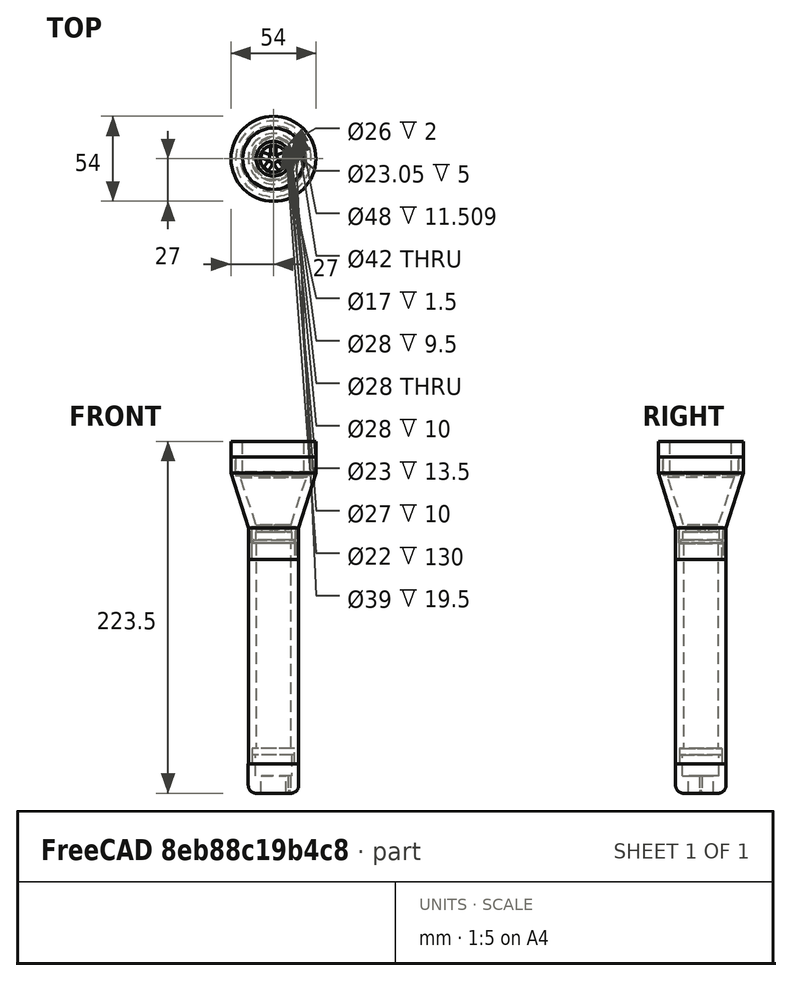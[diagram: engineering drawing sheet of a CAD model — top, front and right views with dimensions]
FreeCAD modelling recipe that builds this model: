
FCSTD DOCUMENT  (FreeCAD 0.19R)
Label: 21mm
License: All rights reserved
LicenseURL: http://en.wikipedia.org/wiki/All_rights_reserved
objects: TechDraw::DrawViewDimension×79, Sketcher::SketchObject×19, PartDesign::Pocket×7, PartDesign::Pad×6, TechDraw::DrawViewPart×6, TechDraw::DrawViewSection×6, PartDesign::Body×5, TechDraw::DrawSVGTemplate×5, TechDraw::DrawPage×5, PartDesign::Plane×3, PartDesign::Hole×3, PartDesign::ShapeBinder×2, PartDesign::Fillet×1, PartDesign::Revolution×1, PartDesign::PolarPattern×1
note: 65 computed .brp shape members not serialized (recipe doc carries the construction recipe); baked Part::Feature solids carry a one-line shape summary decoded from their .brp

FEATURE [Sketcher::SketchObject] Sketch
  MapMode = 5
  Support = -> [XY_Plane]
  sketch-geometry (3):
    g0: Circle CenterX=0 CenterY=0 CenterZ=0 NormalX=0 NormalY=0 NormalZ=1 AngleXU=0 Radius=11
    g1: Circle CenterX=0 CenterY=0 CenterZ=0 NormalX=0 NormalY=0 NormalZ=1 AngleXU=0 Radius=16
    g2: LineSegment [constr] StartX=0 StartY=16.2492 StartZ=0 EndX=0 EndY=22.2492 EndZ=0
  constraints (2):
    c: Radius(g0) = 11
    c: Radius(g1) = 16
FEATURE [PartDesign::Pad] Pad
  Length = 140
  Length2 = 100
  Profile = -> Sketch
  Type = 0
FEATURE [Sketcher::SketchObject] Sketch006
  MapMode = 5
  Placement = pos=(0,0,140) rot=(0,0,1;0rad)
  Support = -> [Pad]
  sketch-geometry (2):
    g0: Circle CenterX=-1e-16 CenterY=0 CenterZ=0 NormalX=0 NormalY=0 NormalZ=1 AngleXU=0 Radius=13.4656
    g1: Circle CenterX=0 CenterY=0 CenterZ=0 NormalX=0 NormalY=0 NormalZ=1 AngleXU=0 Radius=16
FEATURE [PartDesign::Plane] DatumPlane
  AttachmentOffset = pos=(0,-1,0) rot=(0,1,0;1.5708rad)
  Length = 225.248
  MapMode = 5
  Placement = pos=(0,-1,180) rot=(0,1,0;1.5708rad)
  ResizeMode = 0
  Width = 70.2485
FEATURE [Sketcher::SketchObject] Sketch003
  MapMode = 5
  Support = -> [XY_Plane001]
  sketch-geometry (1):
    g0: Circle CenterX=0.0013379 CenterY=-1.51036e-05 CenterZ=0 NormalX=0 NormalY=0 NormalZ=1 AngleXU=0 Radius=16.0028
FEATURE [PartDesign::Pad] Pad001
  Length = 18.5
  Length2 = 100
  Profile = -> Sketch003
  Reversed = true
  Type = 0
FEATURE [Sketcher::SketchObject] Sketch004
  MapMode = 5
  Placement = pos=(0,0,-25) rot=(1,0,0;3.14159rad)
  sketch-geometry (1):
    g0: Circle CenterX=0 CenterY=0 CenterZ=0 NormalX=0 NormalY=0 NormalZ=1 AngleXU=0 Radius=11
  constraints (1):
    c: Radius(g0) = 11  'plugdia'
FEATURE [Sketcher::SketchObject] Sketch005
  MapMode = 5
  Support = -> [Pad001]
  sketch-geometry (1):
    g0: Circle CenterX=0 CenterY=0 CenterZ=0 NormalX=0 NormalY=0 NormalZ=1 AngleXU=0 Radius=13.5
  constraints (1):
    c: Radius(g0) = 13.5
FEATURE [PartDesign::Pad] Pad002
  BaseFeature = -> Pad001
  Length = 6
  Length2 = 100
  Profile = -> Sketch005
  Type = 0
FEATURE [PartDesign::Fillet] Fillet
  Base = -> Pad002 [Edge3]
  BaseFeature = -> Pad002
  Radius = 5
FEATURE [Sketcher::SketchObject] Sketch027
  MapMode = 5
  Placement = pos=(0,0,-18.5) rot=(1,0,0;3.14159rad)
  Support = -> [Fillet]
  sketch-geometry (1):
    g0: Circle CenterX=0 CenterY=0 CenterZ=0 NormalX=0 NormalY=0 NormalZ=1 AngleXU=0 Radius=9.5
  constraints (1):
    c: Radius(g0) = 9.5
FEATURE [PartDesign::Hole] Hole
  BaseFeature = -> Fillet
  Depth = 31
  DepthType = 0
  Diameter = 16
  DrillPoint = 1
  DrillPointAngle = 118
  HoleCutCountersinkAngle = 90
  HoleCutDepth = 0
  HoleCutDiameter = 0
  HoleCutType = 0
  ModelActualThread = false
  Profile = -> Sketch027
  Tapered = false
  TaperedAngle = 90
  ThreadAngle = 0
  ThreadClass = 0
  ThreadCutOffInner = 0
  ThreadCutOffOuter = 0
  ThreadDirection = 0
  ThreadFit = 0
  ThreadPitch = 0
  ThreadSize = 0
  ThreadType = 0
  Threaded = false
FEATURE [Sketcher::SketchObject] Sketch028
  MapMode = 5
  Placement = pos=(0,0,0) rot=(1,0,0;3.14159rad)
  sketch-geometry (1):
    g0: Circle CenterX=0 CenterY=0 CenterZ=0 NormalX=0 NormalY=0 NormalZ=1 AngleXU=0 Radius=13.5
  constraints (1):
    c: Radius(g0) = 13.5
FEATURE [Sketcher::SketchObject] Sketch029
  MapMode = 5
  Placement = pos=(0,0,6) rot=(0,0,1;0rad)
  Support = -> [Hole]
FEATURE [Sketcher::SketchObject] Sketch030
  MapMode = 5
  Placement = pos=(0,0,6) rot=(0,0,1;0rad)
  Support = -> [Hole]
  sketch-geometry (1):
    g0: Circle CenterX=0 CenterY=0 CenterZ=0 NormalX=0 NormalY=0 NormalZ=1 AngleXU=0 Radius=11.5
  constraints (1):
    c: Radius(g0) = 11.5
FEATURE [PartDesign::Pocket] Pocket002
  BaseFeature = -> Hole
  Length = 13.5
  Length2 = 100
  Profile = -> Sketch030
  Type = 0
FEATURE [PartDesign::Pocket] Pocket001
  BaseFeature = -> Pad
  Length = 10
  Length2 = 100
  Profile = -> Sketch028
  Type = 0
FEATURE [PartDesign::Pocket] Pocket
  BaseFeature = -> Pocket001
  Length = 10
  Length2 = 100
  Profile = -> Sketch006
  Type = 0
FEATURE [PartDesign::Body] Body  label="batteryholder"
  Group = -> [Sketch,Pad,Sketch006,DatumPlane,Sketch028,Pocket001,Pocket]
  Origin = -> Origin
  Tip = -> Pocket
FEATURE [PartDesign::ShapeBinder] CopyPocket011
  Placement = pos=(0,-1,180) rot=(0,1,0;1.5708rad)
  TraceSupport = false
FEATURE [PartDesign::ShapeBinder] CopyPocket001
  TraceSupport = false
FEATURE [PartDesign::Plane] DatumPlane001
  AttachmentOffset = pos=(0,0,59) rot=(0,0,1;0rad)
  Length = 64.7976
  MapMode = 5
  Placement = pos=(0,0,249) rot=(0,0,1;0rad)
  ResizeMode = 0
  Support = -> [CopyPocket001]
  Width = 64.7986
FEATURE [Sketcher::SketchObject] Sketch018
  MapMode = 5
  Placement = pos=(0,0,249) rot=(0,0,1;0rad)
  Support = -> [DatumPlane001]
  sketch-geometry (1):
    g0: Circle CenterX=0 CenterY=0 CenterZ=0 NormalX=0 NormalY=0 NormalZ=1 AngleXU=0 Radius=27
  constraints (1):
    c: Radius(g0) = 27
FEATURE [PartDesign::Pad] Pad004
  Length = 10
  Length2 = 100
  Placement = pos=(0,0,249) rot=(0,0,1;0rad)
  Profile = -> Sketch018
  Type = 0
FEATURE [Sketcher::SketchObject] Sketch019
  MapMode = 5
  Placement = pos=(0,0,249) rot=(1,0,0;3.14159rad)
  Support = -> [Pad004]
  sketch-geometry (1):
    g0: Circle CenterX=0 CenterY=0 CenterZ=0 NormalX=0 NormalY=0 NormalZ=1 AngleXU=0 Radius=24
  constraints (1):
    c: Radius(g0) = 24
FEATURE [PartDesign::Pad] Pad005
  BaseFeature = -> Pad004
  Length = 9.5
  Length2 = 100
  Placement = pos=(0,0,249) rot=(0,0,1;0rad)
  Profile = -> Sketch019
  Type = 0
FEATURE [Sketcher::SketchObject] Sketch020
  MapMode = 5
  Placement = pos=(0,0,239.5) rot=(1,0,0;3.14159rad)
  Support = -> [Pad005]
  sketch-geometry (1):
    g0: Circle CenterX=0 CenterY=0 CenterZ=0 NormalX=0 NormalY=0 NormalZ=1 AngleXU=0 Radius=18
  constraints (1):
    c: Radius(g0) = 18
FEATURE [PartDesign::Hole] Hole001
  BaseFeature = -> Pad005
  Depth = 33
  DepthType = 0
  Diameter = 39
  DrillPoint = 1
  DrillPointAngle = 118
  HoleCutCountersinkAngle = 90
  HoleCutDepth = 0
  HoleCutDiameter = 0
  HoleCutType = 0
  ModelActualThread = false
  Placement = pos=(0,0,249) rot=(0,0,1;0rad)
  Profile = -> Sketch020
  Tapered = false
  TaperedAngle = 90
  ThreadAngle = 0
  ThreadClass = 0
  ThreadCutOffInner = 0
  ThreadCutOffOuter = 0
  ThreadDirection = 0
  ThreadFit = 0
  ThreadPitch = 0
  ThreadSize = 0
  ThreadType = 0
  Threaded = false
FEATURE [PartDesign::Body] Body004  label="linseholder001"
  Group = -> [CopyPocket011,DatumPlane001,CopyPocket001,Sketch018,Pad004,Sketch019,Pad005,Sketch020,Hole001]
  Origin = -> Origin004
  Placement = pos=(0,0,-54) rot=(0,0,1;0rad)
  Tip = -> Hole001
FEATURE [Sketcher::SketchObject] Sketch039
  MapMode = 5
  Placement = pos=(0,0,0) rot=(0.57735,0.57735,0.57735;2.0944rad)
  Support = -> [YZ_Plane005]
  sketch-geometry (16):
    g0: LineSegment StartX=27 StartY=195 StartZ=0 EndX=24 EndY=195 EndZ=0
    g1: LineSegment StartX=24 StartY=195 StartZ=0 EndX=24 EndY=183.491 EndZ=0
    g2: LineSegment StartX=24 StartY=183.491 StartZ=0 EndX=21 EndY=183.514 EndZ=0
    g3: LineSegment StartX=21 StartY=183.514 StartZ=0 EndX=21 EndY=182 EndZ=0
    g4: LineSegment StartX=21 StartY=182 StartZ=0 EndX=11 EndY=152 EndZ=0
    g5: LineSegment StartX=11 StartY=152 StartZ=0 EndX=8.5 EndY=152 EndZ=0
    g6: LineSegment StartX=8.5 StartY=152 StartZ=0 EndX=8.5 EndY=150.5 EndZ=0
    g7: LineSegment StartX=8.5 StartY=150.5 StartZ=0 EndX=14 EndY=150.5 EndZ=0
    g8: LineSegment StartX=14 StartY=150.5 StartZ=0 EndX=14 EndY=141 EndZ=0
    g9: LineSegment StartX=14 StartY=141 StartZ=0 EndX=14 EndY=140 EndZ=0
    g10: LineSegment StartX=14 StartY=140 StartZ=0 EndX=14 EndY=130 EndZ=0
    g11: LineSegment StartX=14 StartY=130 StartZ=0 EndX=16 EndY=130 EndZ=0
    g12: LineSegment StartX=16 StartY=130 StartZ=0 EndX=16 EndY=150 EndZ=0
    g13: LineSegment StartX=16 StartY=150 StartZ=0 EndX=27 EndY=185 EndZ=0
    g14: LineSegment StartX=27 StartY=185 StartZ=0 EndX=27 EndY=195 EndZ=0
    g15: LineSegment [constr] StartX=0 StartY=139 StartZ=0 EndX=13 EndY=139 EndZ=0
  constraints (15):
    c: Coincident(g0,g1)
    c: Coincident(g1,g2)
    c: Coincident(g2,g3)
    c: Coincident(g3,g4)
    c: Coincident(g4,g5)
    c: Coincident(g5,g6)
    c: Coincident(g6,g7)
    c: Coincident(g7,g8)
    c: Coincident(g8,g9)
    c: Coincident(g9,g10)
    c: Coincident(g10,g11)
    c: Coincident(g11,g12)
    c: Coincident(g12,g13)
    c: Coincident(g13,g14)
    c: Coincident(g14,g0)
FEATURE [PartDesign::Revolution] Revolution001
  Angle = 360
  Axis = (-3e-16,3e-16,1)
  Base = (0,0,0)
  Placement = pos=(0,0,0) rot=(0.57735,0.57735,0.57735;2.0944rad)
  Profile = -> Sketch039
  ReferenceAxis = -> Z_Axis005
  Reversed = true
FEATURE [PartDesign::Body] Body005  label="flashlighthead"
  Group = -> [Sketch039,Revolution001]
  Origin = -> Origin005
  Tip = -> Revolution001
FEATURE [PartDesign::Plane] DatumPlane002
  Length = 60
  MapMode = 45
  Placement = pos=(-8.73e-14,4.97e-14,150.5) rot=(0,0,1;0rad)
  ResizeMode = 0
  Support = -> [Revolution001]
  Width = 60
FEATURE [Sketcher::SketchObject] Sketch041
  MapMode = 5
  Placement = pos=(-8.73e-14,4.97e-14,150.5) rot=(0,0,1;0rad)
  Support = -> [DatumPlane002]
  sketch-geometry (1):
    g0: Circle CenterX=0 CenterY=0 CenterZ=0 NormalX=0 NormalY=0 NormalZ=1 AngleXU=0 Radius=14.0038
FEATURE [PartDesign::Pad] Pad006
  Length = 10
  Length2 = 100
  Placement = pos=(-1.02e-13,6.8e-14,150.5) rot=(0,0,1;0rad)
  Profile = -> Sketch041
  Reversed = true
  Type = 0
FEATURE [Sketcher::SketchObject] Sketch042
  MapMode = 5
  Placement = pos=(-1.02e-13,6.8e-14,140.5) rot=(1,0,0;3.14159rad)
  Support = -> [Pad006]
  sketch-geometry (1):
    g0: Circle CenterX=0 CenterY=0 CenterZ=0 NormalX=0 NormalY=0 NormalZ=1 AngleXU=0 Radius=13
  constraints (1):
    c: Radius(g0) = 13
FEATURE [PartDesign::Pocket] Pocket003
  BaseFeature = -> Pad006
  Length = 2
  Length2 = 100
  Placement = pos=(-1.02e-13,6.8e-14,150.5) rot=(0,0,1;0rad)
  Profile = -> Sketch042
  Type = 0
FEATURE [Sketcher::SketchObject] Sketch043
  MapMode = 5
  Placement = pos=(-1.02e-13,6.8e-14,142.5) rot=(1,0,0;3.14159rad)
  Support = -> [Pocket003]
  sketch-geometry (1):
    g0: Circle CenterX=0 CenterY=0 CenterZ=0 NormalX=0 NormalY=0 NormalZ=1 AngleXU=0 Radius=11.5274
FEATURE [PartDesign::Pocket] Pocket004
  BaseFeature = -> Pocket003
  Length = 5
  Length2 = 100
  Placement = pos=(-1.02e-13,6.8e-14,150.5) rot=(0,0,1;0rad)
  Profile = -> Sketch043
  Type = 0
FEATURE [Sketcher::SketchObject] Sketch044
  MapMode = 5
  Placement = pos=(-1.02e-13,6.8e-14,147.5) rot=(1,0,0;3.14159rad)
  Support = -> [Pocket004]
  sketch-geometry (4):
    g0: ArcOfCircle CenterX=-1e-16 CenterY=9.70622 CenterZ=0 NormalX=0 NormalY=0 NormalZ=1 AngleXU=0 Radius=1.77733 StartAngle=0 EndAngle=3.14159
    g1: ArcOfCircle CenterX=-1e-16 CenterY=4.33652 CenterZ=0 NormalX=0 NormalY=0 NormalZ=1 AngleXU=0 Radius=1.77733 StartAngle=3.14159 EndAngle=6.28319
    g2: LineSegment StartX=-1.77733 StartY=9.70622 StartZ=0 EndX=-1.77733 EndY=4.33652 EndZ=0
    g3: LineSegment StartX=1.77733 StartY=9.70622 StartZ=0 EndX=1.77733 EndY=4.33652 EndZ=0
  constraints (6):
    c: Tangent(g0,g3) = 1.5708
    c: Tangent(g0,g2) = -1.5708
    c: Tangent(g2,g1) = -1.5708
    c: Tangent(g3,g1) = 1.5708
    c: Vertical(g2)
    c: Equal(g0,g1)
FEATURE [PartDesign::Pocket] Pocket005
  BaseFeature = -> Pocket004
  Length = 5
  Length2 = 100
  Placement = pos=(-1.02e-13,6.8e-14,150.5) rot=(0,0,1;0rad)
  Profile = -> Sketch044
  Type = 0
FEATURE [PartDesign::PolarPattern] PolarPattern
  Angle = 360
  Axis = -> Sketch044 [N_Axis]
  BaseFeature = -> Pocket005
  Occurrences = 5
  Originals = -> [Pocket005]
  Placement = pos=(-1.02e-13,6.8e-14,150.5) rot=(0,0,1;0rad)
FEATURE [Sketcher::SketchObject] Sketch045
  MapMode = 5
  Placement = pos=(-1.02e-13,6.8e-14,150.5) rot=(0,0,1;0rad)
  Support = -> [PolarPattern]
  sketch-geometry (1):
    g0: Circle CenterX=0 CenterY=0 CenterZ=0 NormalX=0 NormalY=0 NormalZ=1 AngleXU=0 Radius=10.25
  constraints (1):
    c: Radius(g0) = 10.25
FEATURE [PartDesign::Pocket] Pocket006
  BaseFeature = -> PolarPattern
  Length = 1
  Length2 = 100
  Placement = pos=(-1.02e-13,6.8e-14,150.5) rot=(0,0,1;0rad)
  Profile = -> Sketch045
  Type = 0
FEATURE [PartDesign::Body] Body006  label="led-holder"
  Group = -> [DatumPlane002,Sketch041,Pad006,Sketch042,Pocket003,Sketch043,Pocket004,Sketch044,Pocket005,PolarPattern,Sketch045,Pocket006]
  Origin = -> Origin006
  Placement = pos=(0,0,0) rot=(0,0,-1;0.628319rad)
  Tip = -> Pocket006
FEATURE [Sketcher::SketchObject] Sketch046
  MapMode = 5
  Placement = pos=(0,0,-7.5) rot=(0,0,1;0rad)
  Support = -> [Pocket002]
  sketch-geometry (1):
    g0: Circle CenterX=10 CenterY=0 CenterZ=0 NormalX=0 NormalY=0 NormalZ=1 AngleXU=0 Radius=1
FEATURE [PartDesign::Hole] Hole002
  BaseFeature = -> Pocket002
  Depth = 10
  DepthType = 0
  Diameter = 1.75
  DrillPoint = 1
  DrillPointAngle = 118
  HoleCutCountersinkAngle = 90
  HoleCutDepth = 0
  HoleCutDiameter = 2
  HoleCutType = 0
  ModelActualThread = false
  Profile = -> Sketch046
  Tapered = false
  TaperedAngle = 90
  ThreadAngle = 60
  ThreadClass = 0
  ThreadCutOffInner = 0.0270633
  ThreadCutOffOuter = 0.0541266
  ThreadDirection = 1
  ThreadFit = 0
  ThreadPitch = 0.25
  ThreadSize = 6
  ThreadType = 2
  Threaded = true
FEATURE [PartDesign::Body] Body001  label="endcap"
  Group = -> [Sketch003,Pad001,Sketch004,Sketch005,Pad002,Fillet,Sketch027,Hole,Sketch029,Sketch030,Pocket002,Sketch046,Hole002]
  Origin = -> Origin001
  Tip = -> Hole002
FEATURE [TechDraw::DrawSVGTemplate] Template
  Height = 841
  Orientation = 1
  Width = 1189
FEATURE [TechDraw::DrawPage] Page
  KeepUpdated = true
  NextBalloonIndex = 1
  ProjectionType = 0
  Template = -> Template
FEATURE [TechDraw::DrawSVGTemplate] Template001
  EditableTexts = APPROVER_NAME=APPROVER NAME; AUTHOR_NAME=AUTHOR NAME; DATE=YYYY-MM-DD; DN=DN; OWNER_NAME=OWNER NAME; PM=PM; PN=PN; REVISION=REV A; RIGHTS=(R) DO NOT DUPLICATE THIS DRAWING TO THIRD PARTIES WITHOUT OWNER'S PERMISSION !; SCALE=M 1:2; SHEET=99 of 99; SIZE=A2; TITLELINE-1=FreeCAD; TOLERANCE=+/- ?
  Height = 420
  Orientation = 1
  Width = 594
FEATURE [TechDraw::DrawViewPart] View  label="Side View"
  CoarseView = false
  Direction = (-1,0,0)
  Focus = 100
  HardHidden = false
  IsoCount = 0
  IsoHidden = false
  IsoVisible = false
  LockPosition = false
  Perspective = false
  Rotation = 0
  Scale = 2
  ScaleType = 0
  SeamHidden = false
  SeamVisible = false
  SmoothHidden = false
  SmoothVisible = false
  Source = -> [Body]
  X = 105.013
  XDirection = (0,-1,0)
  Y = 202.99
FEATURE [TechDraw::DrawViewSection] SectionView  label="Section A - A"
  BaseView = -> View
  CoarseView = false
  CutSurfaceDisplay = 2
  Direction = (0,-1,0)
  FileGeomPattern = <path>
  FileHatchPattern = <path>
  Focus = 100
  FuseBeforeCut = true
  HardHidden = false
  HatchScale = 1
  IsoCount = 0
  IsoHidden = false
  IsoVisible = false
  LockPosition = false
  NameGeomPattern = Diamond
  Perspective = false
  Rotation = 0
  Scale = 2
  ScaleType = 0
  SeamHidden = false
  SeamVisible = false
  SectionDirection = 1
  SectionNormal = (0,-1,0)
  SectionOrigin = (0,0,70)
  SectionSymbol = A
  SmoothHidden = false
  SmoothVisible = false
  Source = -> [Body]
  X = 282.689
  XDirection = (1,0,0)
  Y = 201.911
FEATURE [TechDraw::DrawViewDimension] Dimension
  Arbitrary = false
  FormatSpec = %.1f
  Inverted = false
  LockPosition = false
  MeasureType = 1
  OverTolerance = 0
  References2D = -> [SectionView]
  Rotation = 0
  ScaleType = 0
  TheoreticalExact = false
  Type = 1
  UnderTolerance = 0
  X = -0.880671
  Y = 147.816
FEATURE [TechDraw::DrawViewDimension] Dimension001
  Arbitrary = false
  FormatSpec = %.1f
  Inverted = false
  LockPosition = false
  MeasureType = 1
  OverTolerance = 0
  References2D = -> [SectionView]
  Rotation = 0
  ScaleType = 0
  TheoreticalExact = false
  Type = 1
  UnderTolerance = 0
  X = 0
  Y = 155.302
FEATURE [TechDraw::DrawViewDimension] Dimension002
  Arbitrary = false
  FormatSpec = %.1f
  Inverted = false
  LockPosition = false
  MeasureType = 1
  OverTolerance = 0
  References2D = -> [SectionView]
  Rotation = 0
  ScaleType = 0
  TheoreticalExact = false
  Type = 1
  UnderTolerance = 0
  X = -0.550419
  Y = 164.254
FEATURE [TechDraw::DrawViewDimension] Dimension003
  Arbitrary = false
  FormatSpec = %.1f
  Inverted = false
  LockPosition = false
  MeasureType = 1
  OverTolerance = 0
  References2D = -> [SectionView]
  Rotation = 0
  ScaleType = 0
  TheoreticalExact = false
  Type = 2
  UnderTolerance = 0
  X = -41.1345
  Y = 131.871
FEATURE [TechDraw::DrawViewDimension] Dimension004
  Arbitrary = false
  FormatSpec = %.1f
  Inverted = false
  LockPosition = false
  MeasureType = 1
  OverTolerance = 0
  References2D = -> [SectionView]
  Rotation = 0
  ScaleType = 0
  TheoreticalExact = false
  Type = 2
  UnderTolerance = 0
  X = 44.9505
  Y = 127.768
FEATURE [TechDraw::DrawViewDimension] Dimension005
  Arbitrary = false
  FormatSpec = %.1f
  Inverted = false
  LockPosition = false
  MeasureType = 1
  OverTolerance = 0
  References2D = -> [SectionView]
  Rotation = 0
  ScaleType = 0
  TheoreticalExact = false
  Type = 2
  UnderTolerance = 0
  X = 36.1807
  Y = -0.330252
FEATURE [TechDraw::DrawViewDimension] Dimension006
  Arbitrary = false
  FormatSpec = %.1f
  Inverted = false
  LockPosition = false
  MeasureType = 1
  OverTolerance = 0
  References2D = -> [SectionView]
  Rotation = 0
  ScaleType = 0
  TheoreticalExact = false
  Type = 2
  UnderTolerance = 0
  X = -40.0361
  Y = -9.3395
FEATURE [TechDraw::DrawViewDimension] Dimension007
  Arbitrary = false
  FormatSpec = %.1f
  Inverted = false
  LockPosition = false
  MeasureType = 1
  OverTolerance = 0
  References2D = -> [SectionView]
  Rotation = 0
  ScaleType = 0
  TheoreticalExact = false
  Type = 1
  UnderTolerance = 0
  X = 0.330252
  Y = -150.788
FEATURE [TechDraw::DrawViewDimension] Dimension008
  Arbitrary = false
  FormatSpec = %.1f
  Inverted = false
  LockPosition = false
  MeasureType = 1
  OverTolerance = 0
  References2D = -> [SectionView]
  Rotation = 0
  ScaleType = 0
  TheoreticalExact = false
  Type = 2
  UnderTolerance = 0
  X = -20.9773
  Y = -129.009
FEATURE [TechDraw::DrawViewDimension] Dimension009
  Arbitrary = false
  FormatSpec = %.1f
  Inverted = false
  LockPosition = false
  MeasureType = 1
  OverTolerance = 0
  References2D = -> [SectionView]
  Rotation = 0
  ScaleType = 0
  TheoreticalExact = false
  Type = 1
  UnderTolerance = 0
  X = 0
  Y = -113.725
FEATURE [TechDraw::DrawViewDimension] Dimension010
  Arbitrary = false
  FormatSpec = %.1f
  Inverted = false
  LockPosition = false
  MeasureType = 1
  OverTolerance = 0
  References2D = -> [SectionView]
  Rotation = 0
  ScaleType = 0
  TheoreticalExact = false
  Type = 1
  UnderTolerance = 0
  X = 0.220168
  Y = -157.613
FEATURE [TechDraw::DrawViewDimension] Dimension011
  Arbitrary = false
  FormatSpec = %.1f
  Inverted = false
  LockPosition = false
  MeasureType = 1
  OverTolerance = 0
  References2D = -> [View]
  Rotation = 0
  ScaleType = 0
  TheoreticalExact = false
  Type = 1
  UnderTolerance = 0
  X = 2.85337
  Y = 153.886
FEATURE [TechDraw::DrawViewDimension] Dimension012
  Arbitrary = false
  FormatSpec = %.1f
  Inverted = false
  LockPosition = false
  MeasureType = 1
  OverTolerance = 0
  References2D = -> [View]
  Rotation = 0
  ScaleType = 0
  TheoreticalExact = false
  Type = 2
  UnderTolerance = 0
  X = -42.4009
  Y = 130.951
FEATURE [TechDraw::DrawPage] Page001
  KeepUpdated = true
  NextBalloonIndex = 1
  ProjectionType = 0
  Template = -> Template001
  Views = -> [View,SectionView,Dimension,Dimension001,Dimension002,Dimension003,Dimension004,Dimension005,Dimension006,Dimension007,Dimension008,Dimension009,Dimension010,Dimension011,Dimension012]
FEATURE [TechDraw::DrawSVGTemplate] Template002
  EditableTexts = AUTHOR_NAME=AUTHOR NAME; DN=DN; DRAWING_TITLE=DRAWING TITLE; FC-DATE=DD/MM/YYYY; FC-REV=REV A; FC-SC=SCALE; FC-SH=X / Y; FC-SI=A1; FreeCAD_DRAWING=FreeCAD DRAWING; PN=PN
  Height = 594
  Orientation = 1
  Width = 841
FEATURE [TechDraw::DrawPage] Page002
  KeepUpdated = true
  NextBalloonIndex = 1
  ProjectionType = 0
  Template = -> Template002
FEATURE [TechDraw::DrawSVGTemplate] Template003
  EditableTexts = APPROVER_NAME=APPROVER NAME; AUTHOR_NAME=AUTHOR NAME; DATE=YYYY-MM-DD; DN=DN; OWNER_NAME=OWNER NAME; PM=PM; PN=PN; REVISION=REV A; RIGHTS=(R) DO NOT DUPLICATE THIS DRAWING TO THIRD PARTIES WITHOUT OWNER'S PERMISSION !; SCALE=M 1:2; SHEET=99 of 99; SIZE=A2; TITLELINE-1=FreeCAD; TOLERANCE=+/- ?
  Height = 420
  Orientation = 1
  Width = 594
FEATURE [TechDraw::DrawViewPart] View001  label="Side View   "
  CoarseView = false
  Direction = (-1,0,0)
  Focus = 100
  HardHidden = false
  IsoCount = 0
  IsoHidden = false
  IsoVisible = false
  LockPosition = false
  Perspective = false
  Rotation = 0
  Scale = 2
  ScaleType = 0
  SeamHidden = false
  SeamVisible = false
  SmoothHidden = false
  SmoothVisible = false
  Source = -> [Body005]
  X = 132.111
  XDirection = (0,-1,0)
  Y = 297.733
FEATURE [TechDraw::DrawViewSection] SectionView001  label="Section A - A         "
  BaseView = -> View001
  CoarseView = false
  CutSurfaceDisplay = 2
  Direction = (0,-1,0)
  FileGeomPattern = <path>
  FileHatchPattern = <path>
  Focus = 100
  FuseBeforeCut = true
  HardHidden = false
  HatchScale = 1
  IsoCount = 0
  IsoHidden = false
  IsoVisible = false
  LockPosition = false
  NameGeomPattern = Diamond
  Perspective = false
  Rotation = 0
  Scale = 2
  ScaleType = 0
  SeamHidden = false
  SeamVisible = false
  SectionDirection = 1
  SectionNormal = (0,-1,0)
  SectionOrigin = (0,0,162.5)
  SectionSymbol = A
  SmoothHidden = false
  SmoothVisible = false
  Source = -> [Body005]
  X = 313.191
  XDirection = (1,0,0)
  Y = 297.219
FEATURE [TechDraw::DrawViewDimension] Dimension013
  Arbitrary = false
  FormatSpec = %.1f
  Inverted = false
  LockPosition = false
  MeasureType = 1
  OverTolerance = 0
  References2D = -> [SectionView001]
  Rotation = 0
  ScaleType = 0
  TheoreticalExact = false
  Type = 1
  UnderTolerance = 0
  X = -1.20591
  Y = 80.7974
FEATURE [TechDraw::DrawViewDimension] Dimension014
  Arbitrary = false
  FormatSpec = %.1f
  Inverted = false
  LockPosition = false
  MeasureType = 1
  OverTolerance = 0
  References2D = -> [SectionView001]
  Rotation = 0
  ScaleType = 0
  TheoreticalExact = false
  Type = 1
  UnderTolerance = 0
  X = -2.25746
  Y = 88.0956
FEATURE [TechDraw::DrawViewDimension] Dimension015
  Arbitrary = false
  FormatSpec = %.1f
  Inverted = false
  LockPosition = false
  MeasureType = 1
  OverTolerance = 0
  References2D = -> [View001]
  Rotation = 0
  ScaleType = 0
  TheoreticalExact = false
  Type = 2
  UnderTolerance = 0
  X = 58.1676
  Y = 55
FEATURE [TechDraw::DrawViewDimension] Dimension016
  Arbitrary = false
  FormatSpec = %.1f
  Inverted = false
  LockPosition = false
  MeasureType = 1
  OverTolerance = 0
  References2D = -> [View001]
  Rotation = 0
  ScaleType = 0
  TheoreticalExact = false
  Type = 1
  UnderTolerance = 0
  X = 0.520952
  Y = 76.6346
FEATURE [TechDraw::DrawViewDimension] Dimension017
  Arbitrary = false
  FormatSpec = %.1f
  Inverted = false
  LockPosition = false
  MeasureType = 1
  OverTolerance = 0
  References2D = -> [View001]
  Rotation = 0
  ScaleType = 0
  TheoreticalExact = false
  Type = 1
  UnderTolerance = 0
  X = 0.868254
  Y = -75.0717
FEATURE [TechDraw::DrawViewDimension] Dimension018
  Arbitrary = false
  FormatSpec = %.1f
  Inverted = false
  LockPosition = false
  MeasureType = 1
  OverTolerance = 0
  References2D = -> [View001]
  Rotation = 0
  ScaleType = 0
  TheoreticalExact = false
  Type = 2
  UnderTolerance = 0
  X = 36.3413
  Y = -44.6527
FEATURE [TechDraw::DrawViewDimension] Dimension019
  Arbitrary = false
  FormatSpec = %.1f
  Inverted = false
  LockPosition = false
  MeasureType = 1
  OverTolerance = 0
  References2D = -> [View001]
  Rotation = 0
  ScaleType = 0
  TheoreticalExact = false
  Type = 2
  UnderTolerance = 0
  X = 57.934
  Y = 8.9581
FEATURE [TechDraw::DrawViewDimension] Dimension020
  Arbitrary = false
  FormatSpec = %.1f
  Inverted = false
  LockPosition = false
  MeasureType = 1
  OverTolerance = 0
  References2D = -> [View001]
  Rotation = 0
  ScaleType = 0
  TheoreticalExact = false
  Type = 1
  UnderTolerance = 0
  X = 46.473
  Y = -19.347
FEATURE [TechDraw::DrawViewDimension] Dimension021
  Arbitrary = false
  FormatSpec = %.1f
  Inverted = false
  LockPosition = false
  MeasureType = 1
  OverTolerance = 0
  References2D = -> [SectionView001]
  Rotation = 0
  ScaleType = 0
  TheoreticalExact = false
  Type = 1
  UnderTolerance = 0
  X = -0.264201
  Y = 49.4251
FEATURE [TechDraw::DrawViewDimension] Dimension022
  Arbitrary = false
  FormatSpec = %.1f
  Inverted = false
  LockPosition = false
  MeasureType = 1
  OverTolerance = 0
  References2D = -> [SectionView001]
  Rotation = 0
  ScaleType = 0
  TheoreticalExact = false
  Type = 2
  UnderTolerance = 0
  X = 38.7415
  Y = 49.9149
FEATURE [TechDraw::DrawViewDimension] Dimension023
  Arbitrary = false
  FormatSpec = %.1f
  Inverted = false
  LockPosition = false
  MeasureType = 1
  OverTolerance = 0
  References2D = -> [SectionView001]
  Rotation = 0
  ScaleType = 0
  TheoreticalExact = false
  Type = 2
  UnderTolerance = 0
  X = -45.358
  Y = 54.0189
FEATURE [TechDraw::DrawViewDimension] Dimension024
  Arbitrary = false
  FormatSpec = %.1f
  Inverted = false
  LockPosition = false
  MeasureType = 1
  OverTolerance = 0
  References2D = -> [SectionView001]
  Rotation = 0
  ScaleType = 0
  TheoreticalExact = false
  Type = 1
  UnderTolerance = 0
  X = 9.64335
  Y = -3.56272
FEATURE [TechDraw::DrawViewDimension] Dimension025
  Arbitrary = false
  FormatSpec = %.1f
  Inverted = false
  LockPosition = false
  MeasureType = 1
  OverTolerance = 0
  References2D = -> [SectionView001]
  Rotation = 0
  ScaleType = 0
  TheoreticalExact = false
  Type = 2
  UnderTolerance = 0
  X = 53.4003
  Y = 13.8877
FEATURE [TechDraw::DrawViewDimension] Dimension026
  Arbitrary = false
  FormatSpec = %.1f
  Inverted = false
  LockPosition = false
  MeasureType = 1
  OverTolerance = 0
  References2D = -> [SectionView001]
  Rotation = 0
  ScaleType = 0
  TheoreticalExact = false
  Type = 1
  UnderTolerance = 0
  X = 6.73713
  Y = -28.3593
FEATURE [TechDraw::DrawViewDimension] Dimension027
  Arbitrary = false
  FormatSpec = %.1f
  Inverted = false
  LockPosition = false
  MeasureType = 1
  OverTolerance = 0
  References2D = -> [SectionView001]
  Rotation = 0
  ScaleType = 0
  TheoreticalExact = false
  Type = 2
  UnderTolerance = 0
  X = -12.1123
  Y = -13.253
FEATURE [TechDraw::DrawViewDimension] Dimension028
  Arbitrary = false
  FormatSpec = %.1f
  Inverted = false
  LockPosition = false
  MeasureType = 1
  OverTolerance = 0
  References2D = -> [SectionView001]
  Rotation = 0
  ScaleType = 0
  TheoreticalExact = false
  Type = 1
  UnderTolerance = 0
  X = -0.396302
  Y = -79.7953
FEATURE [TechDraw::DrawViewDimension] Dimension029
  Arbitrary = false
  FormatSpec = %.1f
  Inverted = false
  LockPosition = false
  MeasureType = 1
  OverTolerance = 0
  References2D = -> [SectionView001]
  Rotation = 0
  ScaleType = 0
  TheoreticalExact = false
  Type = 1
  UnderTolerance = 0
  X = 2.24571
  Y = -87.9855
FEATURE [TechDraw::DrawViewDimension] Dimension030
  Arbitrary = false
  FormatSpec = %.1f
  Inverted = false
  LockPosition = false
  MeasureType = 1
  OverTolerance = 0
  References2D = -> [SectionView001]
  Rotation = 0
  ScaleType = 0
  TheoreticalExact = false
  Type = 2
  UnderTolerance = 0
  X = -61.3263
  Y = -44.6037
FEATURE [TechDraw::DrawViewDimension] Dimension031
  Arbitrary = false
  FormatSpec = %.1f
  Inverted = false
  LockPosition = false
  MeasureType = 1
  OverTolerance = 0
  References2D = -> [SectionView001]
  Rotation = 0
  ScaleType = 0
  TheoreticalExact = false
  Type = 2
  UnderTolerance = 0
  X = -61.362
  Y = 9.4716
FEATURE [TechDraw::DrawViewDimension] Dimension032
  Arbitrary = false
  FormatSpec = %.1f
  Inverted = false
  LockPosition = false
  MeasureType = 1
  OverTolerance = 0
  References2D = -> [SectionView001]
  Rotation = 0
  ScaleType = 0
  TheoreticalExact = false
  Type = 2
  UnderTolerance = 0
  X = -61.2655
  Y = 55.9247
FEATURE [TechDraw::DrawViewDimension] Dimension033
  Arbitrary = false
  FormatSpec = %.1f
  Inverted = false
  LockPosition = false
  MeasureType = 1
  OverTolerance = 0
  References2D = -> [SectionView001]
  Rotation = 0
  ScaleType = 0
  TheoreticalExact = false
  Type = 6
  UnderTolerance = 0
  X = -10.436
  Y = 6.47293
FEATURE [TechDraw::DrawViewDimension] Dimension034
  Arbitrary = false
  FormatSpec = %.1f
  Inverted = false
  LockPosition = false
  MeasureType = 1
  OverTolerance = 0
  References2D = -> [SectionView001]
  Rotation = 0
  ScaleType = 0
  TheoreticalExact = false
  Type = 2
  UnderTolerance = 0
  X = -23.5086
  Y = -43.9716
FEATURE [TechDraw::DrawSVGTemplate] Template004
  EditableTexts = APPROVER_NAME=APPROVER NAME; AUTHOR_NAME=AUTHOR NAME; DATE=YYYY-MM-DD; DN=DN; OWNER_NAME=OWNER NAME; PM=PM; PN=PN; REVISION=REV A; RIGHTS=(R) DO NOT DUPLICATE THIS DRAWING TO THIRD PARTIES WITHOUT OWNER'S PERMISSION !; SCALE=M x:x; SHEET=99 of 99; SIZE=A2; TITLELINE-1=FreeCAD; TOLERANCE=+/- ?
  Height = 420
  Orientation = 1
  Width = 594
FEATURE [TechDraw::DrawViewPart] View002  label="Side View lensholder"
  CoarseView = false
  Direction = (-1,0,0)
  Focus = 100
  HardHidden = false
  IsoCount = 0
  IsoHidden = false
  IsoVisible = false
  LockPosition = false
  Perspective = false
  Rotation = 0
  Scale = 2
  ScaleType = 0
  SeamHidden = false
  SeamVisible = false
  SmoothHidden = false
  SmoothVisible = false
  Source = -> [Body004]
  X = 117.626
  XDirection = (0,-1,0)
  Y = 307.067
FEATURE [TechDraw::DrawViewDimension] Dimension035
  Arbitrary = false
  FormatSpec = %.1f
  Inverted = false
  LockPosition = false
  MeasureType = 1
  OverTolerance = 0
  References2D = -> [View002]
  Rotation = 0
  ScaleType = 0
  TheoreticalExact = false
  Type = 1
  UnderTolerance = 0
  X = 0.694603
  Y = -31.6556
FEATURE [TechDraw::DrawViewDimension] Dimension036
  Arbitrary = false
  FormatSpec = %.1f
  Inverted = false
  LockPosition = false
  MeasureType = 1
  OverTolerance = 0
  References2D = -> [View002]
  Rotation = 0
  ScaleType = 0
  TheoreticalExact = false
  Type = 1
  UnderTolerance = 0
  X = -0.347302
  Y = 28.0089
FEATURE [TechDraw::DrawViewDimension] Dimension037
  Arbitrary = false
  FormatSpec = %.1f
  Inverted = false
  LockPosition = false
  MeasureType = 1
  OverTolerance = 0
  References2D = -> [View002]
  Rotation = 0
  ScaleType = 0
  TheoreticalExact = false
  Type = 2
  UnderTolerance = 0
  X = -61.94
  Y = -10.521
FEATURE [TechDraw::DrawViewDimension] Dimension038
  Arbitrary = false
  FormatSpec = %.1f
  Inverted = false
  LockPosition = false
  MeasureType = 1
  OverTolerance = 0
  References2D = -> [View002]
  Rotation = 0
  ScaleType = 0
  TheoreticalExact = false
  Type = 2
  UnderTolerance = 0
  X = -61.8143
  Y = 9.67365
FEATURE [TechDraw::DrawViewSection] SectionView002  label="Section A - A   "
  BaseView = -> View002
  CoarseView = false
  CutSurfaceDisplay = 2
  Direction = (0,-1,0)
  FileGeomPattern = <path>
  FileHatchPattern = <path>
  Focus = 100
  FuseBeforeCut = true
  HardHidden = false
  HatchScale = 1
  IsoCount = 0
  IsoHidden = false
  IsoVisible = false
  LockPosition = false
  NameGeomPattern = Diamond
  Perspective = false
  Rotation = 0
  Scale = 2
  ScaleType = 0
  SeamHidden = false
  SeamVisible = false
  SectionDirection = 1
  SectionNormal = (0,-1,0)
  SectionOrigin = (0,0,195.3)
  SectionSymbol = A
  SmoothHidden = false
  SmoothVisible = false
  Source = -> [Body004]
  X = 292.661
  XDirection = (1,0,0)
  Y = 309.796
FEATURE [TechDraw::DrawViewDimension] Dimension039
  Arbitrary = false
  FormatSpec = %.1f
  Inverted = false
  LockPosition = false
  MeasureType = 1
  OverTolerance = 0
  References2D = -> [SectionView002]
  Rotation = 0
  ScaleType = 0
  TheoreticalExact = false
  Type = 2
  UnderTolerance = 0
  X = 71.7398
  Y = 1.48521
FEATURE [TechDraw::DrawViewDimension] Dimension040
  Arbitrary = false
  FormatSpec = %.1f
  Inverted = false
  LockPosition = false
  MeasureType = 1
  OverTolerance = 0
  References2D = -> [SectionView002]
  Rotation = 0
  ScaleType = 0
  TheoreticalExact = false
  Type = 2
  UnderTolerance = 0
  X = 59.284
  Y = 9.0037
FEATURE [TechDraw::DrawViewDimension] Dimension041
  Arbitrary = false
  FormatSpec = %.1f
  Inverted = false
  LockPosition = false
  MeasureType = 1
  OverTolerance = 0
  References2D = -> [SectionView002]
  Rotation = 0
  ScaleType = 0
  TheoreticalExact = false
  Type = 2
  UnderTolerance = 0
  X = 59.0581
  Y = -11.5531
FEATURE [TechDraw::DrawViewDimension] Dimension042
  Arbitrary = false
  FormatSpec = %.1f
  Inverted = false
  LockPosition = false
  MeasureType = 1
  OverTolerance = 0
  References2D = -> [SectionView002]
  Rotation = 0
  ScaleType = 0
  TheoreticalExact = false
  Type = 1
  UnderTolerance = 0
  X = 1.0568
  Y = 36.8373
FEATURE [TechDraw::DrawViewDimension] Dimension043
  Arbitrary = false
  FormatSpec = %.1f
  Inverted = false
  LockPosition = false
  MeasureType = 1
  OverTolerance = 0
  References2D = -> [SectionView002]
  Rotation = 0
  ScaleType = 0
  TheoreticalExact = false
  Type = 1
  UnderTolerance = 0
  X = 0.264201
  Y = 28.7791
FEATURE [TechDraw::DrawViewDimension] Dimension044
  Arbitrary = false
  FormatSpec = %.1f
  Inverted = false
  LockPosition = false
  MeasureType = 1
  OverTolerance = 0
  References2D = -> [SectionView002]
  Rotation = 0
  ScaleType = 0
  TheoreticalExact = false
  Type = 2
  UnderTolerance = 0
  X = -64.4743
  Y = 0.296302
FEATURE [TechDraw::DrawViewDimension] Dimension045
  Arbitrary = false
  FormatSpec = %.1f
  Inverted = false
  LockPosition = false
  MeasureType = 1
  OverTolerance = 0
  References2D = -> [SectionView002]
  Rotation = 0
  ScaleType = 0
  TheoreticalExact = false
  Type = 1
  UnderTolerance = 0
  X = -43.5
  Y = -24.0914
FEATURE [TechDraw::DrawViewDimension] Dimension046
  Arbitrary = false
  FormatSpec = %.1f
  Inverted = false
  LockPosition = false
  MeasureType = 1
  OverTolerance = 0
  References2D = -> [SectionView002]
  Rotation = 0
  ScaleType = 0
  TheoreticalExact = false
  Type = 1
  UnderTolerance = 0
  X = -46.2358
  Y = 28.7791
FEATURE [TechDraw::DrawViewPart] View003  label="Side View end cap"
  CoarseView = false
  Direction = (-1,0,0)
  Focus = 100
  HardHidden = false
  IsoCount = 0
  IsoHidden = false
  IsoVisible = false
  LockPosition = false
  Perspective = false
  Rotation = 0
  Scale = 2
  ScaleType = 0
  SeamHidden = false
  SeamVisible = false
  SmoothHidden = false
  SmoothVisible = false
  Source = -> [Body001]
  X = 103.404
  XDirection = (0,-1,0)
  Y = 145.152
FEATURE [TechDraw::DrawViewSection] SectionView003  label="Section B - B"
  BaseView = -> View003
  CoarseView = false
  CutSurfaceDisplay = 2
  Direction = (0,-1,0)
  FileGeomPattern = <path>
  FileHatchPattern = <path>
  Focus = 100
  FuseBeforeCut = true
  HardHidden = false
  HatchScale = 1
  IsoCount = 0
  IsoHidden = false
  IsoVisible = false
  LockPosition = false
  NameGeomPattern = Diamond
  Perspective = false
  Rotation = 0
  Scale = 2
  ScaleType = 0
  SeamHidden = false
  SeamVisible = false
  SectionDirection = 1
  SectionNormal = (0,-1,0)
  SectionOrigin = (0.001,0,-6.3)
  SectionSymbol = B
  SmoothHidden = false
  SmoothVisible = false
  Source = -> [Body001]
  X = 227.419
  XDirection = (1,0,0)
  Y = 146.099
FEATURE [TechDraw::DrawViewPart] View004  label="top View"
  CoarseView = false
  Direction = (0,0,1)
  Focus = 100
  HardHidden = false
  IsoCount = 0
  IsoHidden = false
  IsoVisible = false
  LockPosition = false
  Perspective = false
  Rotation = 0
  Scale = 2
  ScaleType = 0
  SeamHidden = false
  SeamVisible = false
  SmoothHidden = false
  SmoothVisible = false
  Source = -> [Body001]
  X = 353.383
  XDirection = (1,0,0)
  Y = 147.287
FEATURE [TechDraw::DrawViewDimension] Dimension047
  Arbitrary = false
  FormatSpec = %.1f
  Inverted = false
  LockPosition = false
  MeasureType = 1
  OverTolerance = 0
  References2D = -> [View003]
  Rotation = 0
  ScaleType = 0
  TheoreticalExact = false
  Type = 1
  UnderTolerance = 0
  X = -1.58524
  Y = 35.9135
FEATURE [TechDraw::DrawViewDimension] Dimension048
  Arbitrary = false
  FormatSpec = %.1f
  Inverted = false
  LockPosition = false
  MeasureType = 1
  OverTolerance = 0
  References2D = -> [View003]
  Rotation = 0
  ScaleType = 0
  TheoreticalExact = false
  Type = 2
  UnderTolerance = 0
  X = 38.0629
  Y = 19.1341
FEATURE [TechDraw::DrawViewDimension] Dimension049
  Arbitrary = false
  FormatSpec = %.1f
  Inverted = false
  LockPosition = false
  MeasureType = 1
  OverTolerance = 0
  References2D = -> [View003]
  Rotation = 0
  ScaleType = 0
  TheoreticalExact = false
  Type = 2
  UnderTolerance = 0
  X = -49.3905
  Y = -1.42669
FEATURE [TechDraw::DrawViewDimension] Dimension050
  Arbitrary = false
  FormatSpec = %.1f
  Inverted = false
  LockPosition = false
  MeasureType = 1
  OverTolerance = 0
  References2D = -> [View003]
  Rotation = 0
  ScaleType = 0
  TheoreticalExact = false
  Type = 2
  UnderTolerance = 0
  X = 37.785
  Y = -6.7926
FEATURE [TechDraw::DrawViewDimension] Dimension051
  Arbitrary = false
  FormatSpec = %.1f
  Inverted = false
  LockPosition = false
  MeasureType = 1
  OverTolerance = 0
  References2D = -> [View003]
  Rotation = 0
  ScaleType = 0
  TheoreticalExact = false
  Type = 2
  UnderTolerance = 0
  X = -40.8827
  Y = -0.841479
FEATURE [TechDraw::DrawViewDimension] Dimension052
  Arbitrary = false
  FormatSpec = %.1f
  Inverted = false
  LockPosition = false
  MeasureType = 1
  OverTolerance = 0
  References2D = -> [SectionView003]
  Rotation = 0
  ScaleType = 0
  TheoreticalExact = false
  Type = 1
  UnderTolerance = 0
  X = 0.156521
  Y = 32.526
FEATURE [TechDraw::DrawViewDimension] Dimension053
  Arbitrary = false
  FormatSpec = %.1f
  Inverted = false
  LockPosition = false
  MeasureType = 1
  OverTolerance = 0
  References2D = -> [SectionView003]
  Rotation = 0
  ScaleType = 0
  TheoreticalExact = false
  Type = 1
  UnderTolerance = 0
  X = -2.06009
  Y = 51.2791
FEATURE [TechDraw::DrawViewDimension] Dimension054
  Arbitrary = false
  FormatSpec = %.1f
  Inverted = false
  LockPosition = false
  MeasureType = 1
  OverTolerance = 0
  References2D = -> [SectionView003]
  Rotation = 0
  ScaleType = 0
  TheoreticalExact = false
  Type = 1
  UnderTolerance = 0
  X = 0.790604
  Y = 40.7691
FEATURE [TechDraw::DrawViewDimension] Dimension055
  Arbitrary = false
  FormatSpec = %.1f
  Inverted = false
  LockPosition = false
  MeasureType = 1
  OverTolerance = 0
  References2D = -> [SectionView003]
  Rotation = 0
  ScaleType = 0
  TheoreticalExact = false
  Type = 2
  UnderTolerance = 0
  X = -19.2818
  Y = 13.1916
FEATURE [TechDraw::DrawViewDimension] Dimension056
  Arbitrary = false
  FormatSpec = %.1f
  Inverted = false
  LockPosition = false
  MeasureType = 1
  OverTolerance = 0
  References2D = -> [SectionView003]
  Rotation = 0
  ScaleType = 0
  TheoreticalExact = false
  Type = 2
  UnderTolerance = 0
  X = -13.4701
  Y = -12.8496
FEATURE [TechDraw::DrawViewDimension] Dimension057
  Arbitrary = false
  FormatSpec = %.1f
  Inverted = false
  LockPosition = false
  MeasureType = 1
  OverTolerance = 0
  References2D = -> [SectionView003]
  Rotation = 0
  ScaleType = 0
  TheoreticalExact = false
  Type = 1
  UnderTolerance = 0
  X = 0.548419
  Y = 3.87478
FEATURE [TechDraw::DrawViewDimension] Dimension058
  Arbitrary = false
  FormatSpec = %.1f
  Inverted = false
  LockPosition = false
  MeasureType = 1
  OverTolerance = 0
  References2D = -> [SectionView003]
  Rotation = 0
  ScaleType = 0
  TheoreticalExact = false
  Type = 1
  UnderTolerance = 0
  X = 19.998
  Y = 3.81099
FEATURE [TechDraw::DrawViewDimension] Dimension059
  Arbitrary = false
  FormatSpec = %.1f
  Inverted = false
  LockPosition = false
  MeasureType = 1
  OverTolerance = 0
  References2D = -> [SectionView003]
  Rotation = 0
  ScaleType = 0
  TheoreticalExact = false
  Type = 2
  UnderTolerance = 0
  X = -43.0836
  Y = -0.498031
FEATURE [TechDraw::DrawViewDimension] Dimension060
  Arbitrary = false
  FormatSpec = %.1f
  Inverted = false
  LockPosition = false
  MeasureType = 1
  OverTolerance = 0
  References2D = -> [SectionView003]
  Rotation = 0
  ScaleType = 0
  TheoreticalExact = false
  Type = 1
  UnderTolerance = 0
  X = -26.7034
  Y = -36.0059
FEATURE [TechDraw::DrawViewDimension] Dimension061
  Arbitrary = false
  FormatSpec = R%.1f
  Inverted = false
  LockPosition = false
  MeasureType = 1
  OverTolerance = 0
  References2D = -> [SectionView003]
  Rotation = 0
  ScaleType = 0
  TheoreticalExact = false
  Type = 4
  UnderTolerance = 0
  X = -36.7802
  Y = -23.1132
FEATURE [TechDraw::DrawViewDimension] Dimension062
  Arbitrary = false
  FormatSpec = R%.1f
  Inverted = false
  LockPosition = false
  MeasureType = 1
  OverTolerance = 0
  References2D = -> [SectionView003]
  Rotation = 0
  ScaleType = 0
  TheoreticalExact = false
  Type = 4
  UnderTolerance = 0
  X = 39.6945
  Y = -22.0078
FEATURE [TechDraw::DrawViewDimension] Dimension063
  Arbitrary = false
  FormatSpec = %.1f
  Inverted = false
  LockPosition = false
  MeasureType = 1
  OverTolerance = 0
  References2D = -> [View004]
  Rotation = 0
  ScaleType = 0
  TheoreticalExact = false
  Type = 1
  UnderTolerance = 0
  X = 8.79142
  Y = 3.41677
FEATURE [TechDraw::DrawViewDimension] Dimension064
  Arbitrary = false
  FormatSpec = ⌀%.1f
  Inverted = false
  LockPosition = false
  MeasureType = 1
  OverTolerance = 0
  References2D = -> [View004]
  Rotation = 0
  ScaleType = 0
  TheoreticalExact = false
  Type = 5
  UnderTolerance = 0
  X = 7.79281
  Y = -5.40844
FEATURE [TechDraw::DrawViewDimension] Dimension065
  Arbitrary = false
  FormatSpec = %.1f
  Inverted = false
  LockPosition = false
  MeasureType = 1
  OverTolerance = 0
  References2D = -> [SectionView003]
  Rotation = 0
  ScaleType = 0
  TheoreticalExact = false
  Type = 2
  UnderTolerance = 0
  X = 16.8169
  Y = -11.7642
FEATURE [TechDraw::DrawPage] Page004
  KeepUpdated = true
  NextBalloonIndex = 1
  ProjectionType = 0
  Template = -> Template004
  Views = -> [View002,Dimension035,Dimension036,Dimension037,Dimension038,SectionView002,Dimension039,Dimension040,Dimension041,Dimension042,Dimension043,Dimension044,Dimension045,Dimension046,View003,SectionView003,View004,Dimension047,Dimension048,Dimension049,Dimension050,Dimension051,Dimension052,Dimension053,Dimension054,Dimension055,Dimension056,Dimension057,Dimension058,Dimension059,Dimension060,+5 more]
FEATURE [TechDraw::DrawViewPart] View005  label="side View led holder"
  CoarseView = false
  Direction = (0,-1,0)
  Focus = 100
  HardHidden = false
  IsoCount = 0
  IsoHidden = false
  IsoVisible = false
  LockPosition = false
  Perspective = false
  Rotation = 0
  Scale = 2
  ScaleType = 0
  SeamHidden = false
  SeamVisible = false
  SmoothHidden = false
  SmoothVisible = false
  Source = -> [Body006]
  X = 128.7
  XDirection = (1,0,0)
  Y = 118.878
FEATURE [TechDraw::DrawViewSection] SectionView005  label="Section C - C"
  BaseView = -> View005
  CoarseView = false
  CutSurfaceDisplay = 2
  Direction = (0,0,-1)
  FileGeomPattern = <path>
  FileHatchPattern = <path>
  Focus = 100
  FuseBeforeCut = true
  HardHidden = false
  HatchScale = 1
  IsoCount = 0
  IsoHidden = false
  IsoVisible = false
  LockPosition = false
  NameGeomPattern = Diamond
  Perspective = false
  Rotation = 0
  Scale = 2
  ScaleType = 0
  SeamHidden = false
  SeamVisible = false
  SectionDirection = 2
  SectionNormal = (0,0,-1)
  SectionOrigin = (0,0,145.5)
  SectionSymbol = C
  SmoothHidden = false
  SmoothVisible = false
  Source = -> [Body006]
  X = 216.342
  XDirection = (1,0,0)
  Y = 97.6543
FEATURE [TechDraw::DrawViewDimension] Dimension066
  Arbitrary = false
  FormatSpec = %.1f
  Inverted = false
  LockPosition = false
  MeasureType = 1
  OverTolerance = 0
  References2D = -> [View005]
  Rotation = 0
  ScaleType = 0
  TheoreticalExact = false
  Type = 2
  UnderTolerance = 0
  X = -44.3881
  Y = -0.660503
FEATURE [TechDraw::DrawViewDimension] Dimension067
  Arbitrary = false
  FormatSpec = %.1f
  Inverted = false
  LockPosition = false
  MeasureType = 1
  OverTolerance = 0
  References2D = -> [View005]
  Rotation = 0
  ScaleType = 0
  TheoreticalExact = false
  Type = 1
  UnderTolerance = 0
  X = 1.18891
  Y = 22.4175
FEATURE [TechDraw::DrawViewDimension] Dimension068
  Arbitrary = false
  FormatSpec = %.1f
  Inverted = false
  LockPosition = false
  MeasureType = 1
  OverTolerance = 0
  References2D = -> [SectionView005]
  Rotation = 0
  ScaleType = 0
  TheoreticalExact = false
  Type = 0
  UnderTolerance = 0
  X = -16.2362
  Y = 4.45669
FEATURE [TechDraw::DrawViewDimension] Dimension069
  Arbitrary = false
  FormatSpec = %.1f
  Inverted = false
  LockPosition = false
  MeasureType = 1
  OverTolerance = 0
  References2D = -> [SectionView005]
  Rotation = 0
  ScaleType = 0
  TheoreticalExact = false
  Type = 0
  UnderTolerance = 0
  X = -6.00702
  Y = 1.9161
FEATURE [TechDraw::DrawViewDimension] Dimension071
  Arbitrary = false
  FormatSpec = %.1f
  Inverted = false
  LockPosition = false
  MeasureType = 1
  OverTolerance = 0
  References2D = -> [SectionView005]
  Rotation = 0
  ScaleType = 0
  TheoreticalExact = false
  Type = 0
  UnderTolerance = 0
  X = -2.42595
  Y = 32.6701
FEATURE [TechDraw::DrawViewSection] SectionView006  label="Section D - D"
  BaseView = -> View005
  CoarseView = false
  CutSurfaceDisplay = 2
  Direction = (1,0,0)
  FileGeomPattern = <path>
  FileHatchPattern = <path>
  Focus = 100
  FuseBeforeCut = true
  HardHidden = false
  HatchScale = 1
  IsoCount = 0
  IsoHidden = false
  IsoVisible = false
  LockPosition = false
  NameGeomPattern = Diamond
  Perspective = false
  Rotation = 0
  Scale = 2
  ScaleType = 0
  SeamHidden = false
  SeamVisible = false
  SectionDirection = 1
  SectionNormal = (1,0,0)
  SectionOrigin = (0,0,145.5)
  SectionSymbol = D
  SmoothHidden = false
  SmoothVisible = false
  Source = -> [Body006]
  X = 127.168
  XDirection = (0,1,0)
  Y = 72.1172
FEATURE [TechDraw::DrawViewDimension] Dimension072
  Arbitrary = false
  FormatSpec = %.1f
  Inverted = false
  LockPosition = false
  MeasureType = 1
  OverTolerance = 0
  References2D = -> [SectionView006]
  Rotation = 0
  ScaleType = 0
  TheoreticalExact = false
  Type = 1
  UnderTolerance = 0
  X = -1.19257
  Y = -26.0539
FEATURE [TechDraw::DrawViewDimension] Dimension073
  Arbitrary = false
  FormatSpec = %.1f
  Inverted = false
  LockPosition = false
  MeasureType = 1
  OverTolerance = 0
  References2D = -> [SectionView006]
  Rotation = 0
  ScaleType = 0
  TheoreticalExact = false
  Type = 2
  UnderTolerance = 0
  X = 16.3334
  Y = -2.59718
FEATURE [TechDraw::DrawViewDimension] Dimension074
  Arbitrary = false
  FormatSpec = %.1f
  Inverted = false
  LockPosition = false
  MeasureType = 1
  OverTolerance = 0
  References2D = -> [SectionView006]
  Rotation = 0
  ScaleType = 0
  TheoreticalExact = false
  Type = 2
  UnderTolerance = 0
  X = -19.9358
  Y = -1.27521
FEATURE [TechDraw::DrawViewDimension] Dimension075
  Arbitrary = false
  FormatSpec = %.1f
  Inverted = false
  LockPosition = false
  MeasureType = 1
  OverTolerance = 0
  References2D = -> [SectionView006]
  Rotation = 0
  ScaleType = 0
  TheoreticalExact = false
  Type = 1
  UnderTolerance = 0
  X = -6.9818
  Y = -20.2119
FEATURE [TechDraw::DrawViewDimension] Dimension076
  Arbitrary = false
  FormatSpec = R%.1f
  Inverted = false
  LockPosition = false
  MeasureType = 1
  OverTolerance = 0
  References2D = -> [SectionView005]
  Rotation = 0
  ScaleType = 0
  TheoreticalExact = false
  Type = 4
  UnderTolerance = 0
  X = -24.2187
  Y = -26.53
FEATURE [TechDraw::DrawViewDimension] Dimension077
  Arbitrary = false
  FormatSpec = R%.1f
  Inverted = false
  LockPosition = false
  MeasureType = 1
  OverTolerance = 0
  References2D = -> [SectionView005]
  Rotation = 0
  ScaleType = 0
  TheoreticalExact = false
  Type = 4
  UnderTolerance = 0
  X = -33.4456
  Y = -7.38989
FEATURE [TechDraw::DrawViewDimension] Dimension078
  Arbitrary = false
  FormatSpec = %.1f
  Inverted = false
  LockPosition = false
  MeasureType = 1
  OverTolerance = 0
  References2D = -> [SectionView006]
  Rotation = 0
  ScaleType = 0
  TheoreticalExact = false
  Type = 2
  UnderTolerance = 0
  X = -25.5455
  Y = 17.0269
FEATURE [TechDraw::DrawViewDimension] Dimension079
  Arbitrary = false
  FormatSpec = %.1f
  Inverted = false
  LockPosition = false
  MeasureType = 1
  OverTolerance = 0
  References2D = -> [SectionView006]
  Rotation = 0
  ScaleType = 0
  TheoreticalExact = false
  Type = 1
  UnderTolerance = 0
  X = -10.5048
  Y = 21.5308
FEATURE [TechDraw::DrawPage] Page003
  KeepUpdated = true
  NextBalloonIndex = 1
  ProjectionType = 0
  Template = -> Template003
  Views = -> [View001,SectionView001,Dimension013,Dimension014,Dimension015,Dimension016,Dimension017,Dimension018,Dimension019,Dimension020,Dimension021,Dimension022,Dimension023,Dimension024,Dimension025,Dimension026,Dimension027,Dimension028,Dimension029,Dimension030,Dimension031,Dimension032,Dimension033,Dimension034,View005,SectionView005,Dimension066,Dimension067,Dimension068,Dimension069,Dimension071,+9 more]
note: 12 file-system paths scrubbed to <path> (originals preserved in the JSON sidecar)
